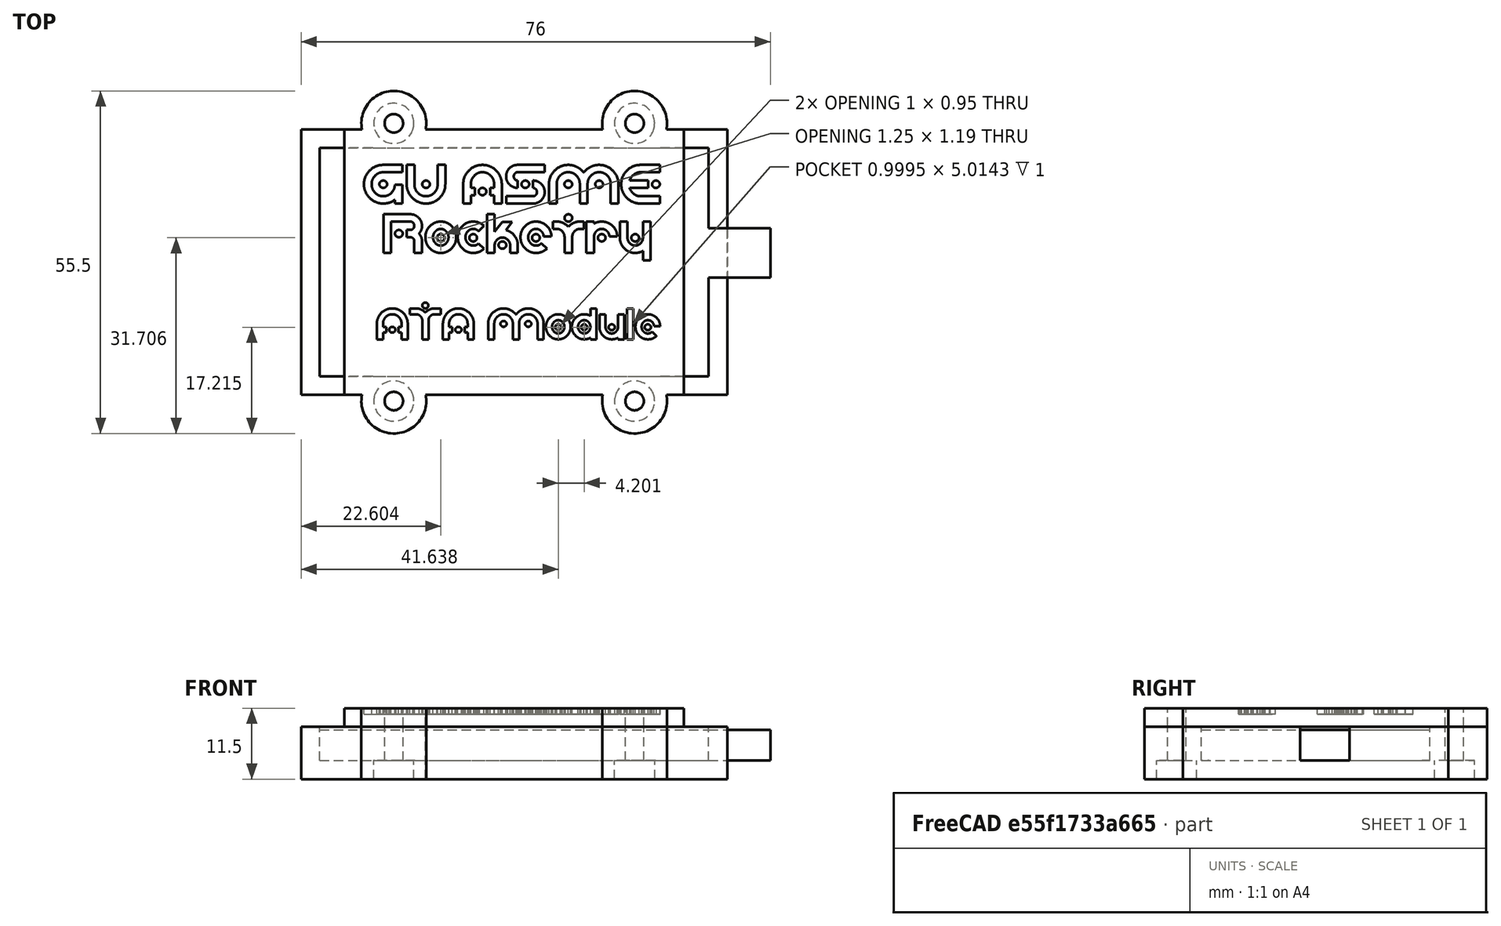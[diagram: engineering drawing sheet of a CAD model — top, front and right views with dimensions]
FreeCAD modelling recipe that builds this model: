
FCSTD DOCUMENT  (FreeCAD 0.19R)
Label: BatteryPlate
License: All rights reserved
LicenseURL: http://en.wikipedia.org/wiki/All_rights_reserved
objects: Part::Cylinder×32, Part::MultiFuse×18, Part::Cut×13, Part::Box×8, Part::Part2DObjectPython×3, Part::Extrusion×3
note: 77 computed .brp shape members not serialized (recipe doc carries the construction recipe); baked Part::Feature solids carry a one-line shape summary decoded from their .brp

FEATURE [Part::Box] Box  label="Cube"
  AttacherType = Attacher::AttachEngine3D
  Height = 6
  Length = 63
  Width = 37
FEATURE [Part::Box] Box001  label="Cube001"
  AttacherType = Attacher::AttachEngine3D
  Height = 6
  Length = 10
  Placement = pos=(63,16,0) rot=(0,0,1;0rad)
  Width = 8
FEATURE [Part::MultiFuse] Fusion  label="Battery Model"
  Placement = pos=(3,3,3) rot=(0,0,1;0rad)
  Shapes = -> [Box001,Box]
FEATURE [Part::Box] Box002  label="Cube002"
  AttacherType = Attacher::AttachEngine3D
  Height = 8.5
  Length = 69
  Width = 43
FEATURE [Part::Cut] Cut
  Base = -> Box002
  Tool = -> Fusion
FEATURE [Part::Box] Box003  label="Cube003"
  AttacherType = Attacher::AttachEngine3D
  Height = 5
  Length = 10
  Placement = pos=(63,16,0) rot=(0,0,1;0rad)
  Width = 8
FEATURE [Part::Box] Box004  label="Cube004"
  AttacherType = Attacher::AttachEngine3D
  Height = 5
  Length = 63
  Width = 37
FEATURE [Part::MultiFuse] Fusion001  label="Battery Model001"
  Placement = pos=(3,3,3) rot=(0,0,1;0rad)
  Shapes = -> [Box003,Box004]
FEATURE [Part::Cylinder] Cylinder008
  Angle = 360
  AttacherType = Attacher::AttachEngine3D
  Height = 8.5
  Placement = pos=(15,-1,0) rot=(0,0,1;0rad)
  Radius = 5.25
FEATURE [Part::Box] Box005  label="Lid Plate Base"
  AttacherType = Attacher::AttachEngine3D
  Height = 3
  Length = 55
  Placement = pos=(7,0,8.5) rot=(0,0,1;0rad)
  Width = 43
FEATURE [Part::Cylinder] Cylinder009  label="Screw Shaft"
  Angle = 360
  AttacherType = Attacher::AttachEngine3D
  Height = 8.5
  Placement = pos=(15,-1,0) rot=(0,0,1;0rad)
  Radius = 1.5
FEATURE [Part::Cylinder] Cylinder010  label="Nut Recess"
  Angle = 360
  AttacherType = Attacher::AttachEngine3D
  Height = 3
  Placement = pos=(15,-1,0) rot=(0,0,1;0rad)
  Radius = 3.25
FEATURE [Part::Cylinder] Cylinder012  label="Lid Flange Material"
  Angle = 360
  AttacherType = Attacher::AttachEngine3D
  Height = 3
  Placement = pos=(15,-1,8.5) rot=(0,0,1;0rad)
  Radius = 5.25
FEATURE [Part::MultiFuse] Fusion002  label="Base Bolt Assembly"
  Shapes = -> [Cylinder009,Cylinder010]
FEATURE [Part::Cut] Cut002  label="Base Bolt Flange - LL"
  Base = -> Cylinder008
  Tool = -> Fusion002
FEATURE [Part::Cylinder] Cylinder013  label="Screw Shaft001"
  Angle = 360
  AttacherType = Attacher::AttachEngine3D
  Height = 8.5
  Placement = pos=(15,-1,0) rot=(0,0,1;0rad)
  Radius = 1.5
FEATURE [Part::Cylinder] Cylinder014  label="Nut Recess001"
  Angle = 360
  AttacherType = Attacher::AttachEngine3D
  Height = 3
  Placement = pos=(15,-1,0) rot=(0,0,1;0rad)
  Radius = 3.25
FEATURE [Part::MultiFuse] Fusion003  label="Base Bolt Assembly001"
  Shapes = -> [Cylinder013,Cylinder014]
FEATURE [Part::Cylinder] Cylinder015
  Angle = 360
  AttacherType = Attacher::AttachEngine3D
  Height = 8.5
  Placement = pos=(15,-1,0) rot=(0,0,1;0rad)
  Radius = 5.25
FEATURE [Part::Cut] Cut004  label="Base Bolt Flange - LR"
  Base = -> Cylinder015
  Placement = pos=(39,0,0) rot=(0,0,1;0rad)
  Tool = -> Fusion003
FEATURE [Part::Cylinder] Cylinder016  label="Nut Recess002"
  Angle = 360
  AttacherType = Attacher::AttachEngine3D
  Height = 3
  Placement = pos=(15,-1,0) rot=(0,0,1;0rad)
  Radius = 3.25
FEATURE [Part::Cylinder] Cylinder017  label="Screw Shaft002"
  Angle = 360
  AttacherType = Attacher::AttachEngine3D
  Height = 8.5
  Placement = pos=(15,-1,0) rot=(0,0,1;0rad)
  Radius = 1.5
FEATURE [Part::Cylinder] Cylinder018
  Angle = 360
  AttacherType = Attacher::AttachEngine3D
  Height = 8.5
  Placement = pos=(15,-1,0) rot=(0,0,1;0rad)
  Radius = 5.25
FEATURE [Part::MultiFuse] Fusion004  label="Base Bolt Assembly002"
  Shapes = -> [Cylinder017,Cylinder016]
FEATURE [Part::Cut] Cut005  label="Base Bolt Flange - UR"
  Base = -> Cylinder018
  Placement = pos=(39,45,0) rot=(0,0,1;0rad)
  Tool = -> Fusion004
FEATURE [Part::Cylinder] Cylinder019
  Angle = 360
  AttacherType = Attacher::AttachEngine3D
  Height = 8.5
  Placement = pos=(15,-1,0) rot=(0,0,1;0rad)
  Radius = 5.25
FEATURE [Part::Cylinder] Cylinder020  label="Screw Shaft003"
  Angle = 360
  AttacherType = Attacher::AttachEngine3D
  Height = 8.5
  Placement = pos=(15,-1,0) rot=(0,0,1;0rad)
  Radius = 1.5
FEATURE [Part::Cylinder] Cylinder021  label="Nut Recess003"
  Angle = 360
  AttacherType = Attacher::AttachEngine3D
  Height = 3
  Placement = pos=(15,-1,0) rot=(0,0,1;0rad)
  Radius = 3.25
FEATURE [Part::MultiFuse] Fusion005  label="Base Bolt Assembly003"
  Shapes = -> [Cylinder020,Cylinder021]
FEATURE [Part::Cut] Cut006  label="Base Bolt Flange - UL"
  Base = -> Cylinder019
  Placement = pos=(0,45,0) rot=(0,0,1;0rad)
  Tool = -> Fusion005
FEATURE [Part::Cylinder] Cylinder022  label="Screw Shaft004"
  Angle = 360
  AttacherType = Attacher::AttachEngine3D
  Height = 8.5
  Placement = pos=(15,-1,0) rot=(0,0,1;0rad)
  Radius = 1.5
FEATURE [Part::Cylinder] Cylinder023  label="Nut Recess004"
  Angle = 360
  AttacherType = Attacher::AttachEngine3D
  Height = 3
  Placement = pos=(15,-1,0) rot=(0,0,1;0rad)
  Radius = 3.25
FEATURE [Part::MultiFuse] Fusion006  label="Base Bolt Assembly - LL"
  Shapes = -> [Cylinder022,Cylinder023]
FEATURE [Part::Cylinder] Cylinder024  label="Screw Shaft005"
  Angle = 360
  AttacherType = Attacher::AttachEngine3D
  Height = 8.5
  Placement = pos=(15,-1,0) rot=(0,0,1;0rad)
  Radius = 1.5
FEATURE [Part::Cylinder] Cylinder025  label="Nut Recess005"
  Angle = 360
  AttacherType = Attacher::AttachEngine3D
  Height = 3
  Placement = pos=(15,-1,0) rot=(0,0,1;0rad)
  Radius = 3.25
FEATURE [Part::MultiFuse] Fusion007  label="Base Bolt Assembly - LR"
  Placement = pos=(39,0,0) rot=(0,0,1;0rad)
  Shapes = -> [Cylinder024,Cylinder025]
FEATURE [Part::Cylinder] Cylinder026  label="Nut Recess006"
  Angle = 360
  AttacherType = Attacher::AttachEngine3D
  Height = 3
  Placement = pos=(15,-1,0) rot=(0,0,1;0rad)
  Radius = 3.25
FEATURE [Part::Cylinder] Cylinder027  label="Screw Shaft006"
  Angle = 360
  AttacherType = Attacher::AttachEngine3D
  Height = 8.5
  Placement = pos=(15,-1,0) rot=(0,0,1;0rad)
  Radius = 1.5
FEATURE [Part::MultiFuse] Fusion008  label="Base Bolt Assembly - UR"
  Placement = pos=(39,45,0) rot=(0,0,1;0rad)
  Shapes = -> [Cylinder027,Cylinder026]
FEATURE [Part::Cylinder] Cylinder028  label="Screw Shaft007"
  Angle = 360
  AttacherType = Attacher::AttachEngine3D
  Height = 8.5
  Placement = pos=(15,-1,0) rot=(0,0,1;0rad)
  Radius = 1.5
FEATURE [Part::Cylinder] Cylinder029  label="Nut Recess007"
  Angle = 360
  AttacherType = Attacher::AttachEngine3D
  Height = 3
  Placement = pos=(15,-1,0) rot=(0,0,1;0rad)
  Radius = 3.25
FEATURE [Part::MultiFuse] Fusion009  label="Base Bolt Assembly - UL"
  Placement = pos=(0,45,0) rot=(0,0,1;0rad)
  Shapes = -> [Cylinder028,Cylinder029]
FEATURE [Part::MultiFuse] Fusion010  label="Base Bolt Remove Assembly"
  Shapes = -> [Fusion009,Fusion006,Fusion007,Fusion008]
FEATURE [Part::Cut] Cut007
  Base = -> Cut
  Tool = -> Fusion010
FEATURE [Part::MultiFuse] Fusion011  label="Base Bolt Assemblies"
  Shapes = -> [Cut006,Cut005,Cut004,Cut002]
FEATURE [Part::Box] Box006  label="Cube005"
  AttacherType = Attacher::AttachEngine3D
  Height = 5.5
  Length = 10
  Placement = pos=(63,16,0) rot=(0,0,1;0rad)
  Width = 8
FEATURE [Part::Box] Box007  label="Cube006"
  AttacherType = Attacher::AttachEngine3D
  Height = 5.5
  Length = 63
  Width = 37
FEATURE [Part::MultiFuse] Fusion012  label="Battery Model002"
  Placement = pos=(3,3,3) rot=(0,0,1;0rad)
  Shapes = -> [Box006,Box007]
FEATURE [Part::Cut] Cut008  label="Base Bolt Assemblies - no Bat"
  Base = -> Fusion011
  Tool = -> Fusion012
FEATURE [Part::MultiFuse] Fusion013  label="Base Initial"
  Shapes = -> [Cut007,Cut008]
FEATURE [Part::Cylinder] Cylinder030  label="Lid Bolt Hole001"
  Angle = 360
  AttacherType = Attacher::AttachEngine3D
  Height = 3
  Placement = pos=(15,-1,8.5) rot=(0,0,1;0rad)
  Radius = 1.5
FEATURE [Part::Cylinder] Cylinder031  label="Lid Bolt Hole002"
  Angle = 360
  AttacherType = Attacher::AttachEngine3D
  Height = 3
  Placement = pos=(54,-1,8.5) rot=(0,0,1;0rad)
  Radius = 1.5
FEATURE [Part::Cylinder] Cylinder032  label="Lid Bolt Hole003"
  Angle = 360
  AttacherType = Attacher::AttachEngine3D
  Height = 3
  Placement = pos=(54,44,8.5) rot=(0,0,1;0rad)
  Radius = 1.5
FEATURE [Part::Cylinder] Cylinder033  label="Lid Bolt Hole004"
  Angle = 360
  AttacherType = Attacher::AttachEngine3D
  Height = 3
  Placement = pos=(15,44,8.5) rot=(0,0,1;0rad)
  Radius = 1.5
FEATURE [Part::MultiFuse] Fusion014  label="Lid Base Bolt Holes for Cut"
  Shapes = -> [Cylinder033,Cylinder030,Cylinder031,Cylinder032]
FEATURE [Part::Cylinder] Cylinder011  label="Lid Bolt Hole"
  Angle = 360
  AttacherType = Attacher::AttachEngine3D
  Height = 3
  Placement = pos=(15,-1,8.5) rot=(0,0,1;0rad)
  Radius = 1.5
FEATURE [Part::Cut] Cut001  label="Lid Bolt Flange - LL"
  Base = -> Cylinder012
  Tool = -> Cylinder011
FEATURE [Part::Cut] Cut009
  Base = -> Box005
  Tool = -> Fusion014
FEATURE [Part::Cylinder] Cylinder034  label="Lid Bolt Hole005"
  Angle = 360
  AttacherType = Attacher::AttachEngine3D
  Height = 3
  Placement = pos=(15,-1,8.5) rot=(0,0,1;0rad)
  Radius = 1.5
FEATURE [Part::Cylinder] Cylinder035  label="Lid Flange Material001"
  Angle = 360
  AttacherType = Attacher::AttachEngine3D
  Height = 3
  Placement = pos=(15,-1,8.5) rot=(0,0,1;0rad)
  Radius = 5.25
FEATURE [Part::Cut] Cut010  label="Lid Bolt Flange - LR"
  Base = -> Cylinder035
  Placement = pos=(39,0,0) rot=(0,0,1;0rad)
  Tool = -> Cylinder034
FEATURE [Part::Cylinder] Cylinder036  label="Lid Bolt Hole006"
  Angle = 360
  AttacherType = Attacher::AttachEngine3D
  Height = 3
  Placement = pos=(15,-1,8.5) rot=(0,0,1;0rad)
  Radius = 1.5
FEATURE [Part::Cylinder] Cylinder037  label="Lid Flange Material002"
  Angle = 360
  AttacherType = Attacher::AttachEngine3D
  Height = 3
  Placement = pos=(15,-1,8.5) rot=(0,0,1;0rad)
  Radius = 5.25
FEATURE [Part::Cut] Cut011  label="Lid Bolt Flange - UR"
  Base = -> Cylinder037
  Placement = pos=(39,45,0) rot=(0,0,1;0rad)
  Tool = -> Cylinder036
FEATURE [Part::Cylinder] Cylinder038  label="Lid Flange Material003"
  Angle = 360
  AttacherType = Attacher::AttachEngine3D
  Height = 3
  Placement = pos=(15,-1,8.5) rot=(0,0,1;0rad)
  Radius = 5.25
FEATURE [Part::Cylinder] Cylinder039  label="Lid Bolt Hole007"
  Angle = 360
  AttacherType = Attacher::AttachEngine3D
  Height = 3
  Placement = pos=(15,-1,8.5) rot=(0,0,1;0rad)
  Radius = 1.5
FEATURE [Part::Cut] Cut012  label="Lid Bolt Flange - UL"
  Base = -> Cylinder038
  Placement = pos=(0,45,0) rot=(0,0,1;0rad)
  Tool = -> Cylinder039
FEATURE [Part::MultiFuse] Fusion015  label="Lid Bolt Flanges"
  Shapes = -> [Cut001,Cut010,Cut011,Cut012]
FEATURE [Part::MultiFuse] Fusion016  label="Lid"
  Shapes = -> [Cut009,Fusion015]
FEATURE [Part::Part2DObjectPython] ShapeString  # Draft 2D object (typed FeaturePython)
  FontFile = <userpath>/fonts/SFPlanetaryOrbiter.ttf
  Placement = pos=(-50,20,0) rot=(0,0,1;0rad)
  Size = 5
  String = GU ASME
  Tracking = 0
FEATURE [Part::Part2DObjectPython] ShapeString001  # Draft 2D object (typed FeaturePython)
  FontFile = <userpath>/fonts/SFPlanetaryOrbiter.ttf
  Placement = pos=(-50,10,0) rot=(0,0,1;0rad)
  Size = 5
  String = Rocketry
  Tracking = 0
FEATURE [Part::Part2DObjectPython] ShapeString002  # Draft 2D object (typed FeaturePython)
  FontFile = <userpath>/fonts/SFPlanetaryOrbiter.ttf
  Placement = pos=(-50,0,0) rot=(0,0,1;0rad)
  Size = 4
  String = ATA Module
  Tracking = 0
FEATURE [Part::Extrusion] Extrude
  Base = -> ShapeString
  Dir = (0,0,1)
  DirMode = 2
  FaceMakerClass = Part::FaceMakerBullseye
  LengthFwd = 1
  LengthRev = 0
  Placement = pos=(60,11,10.5) rot=(0,0,1;0rad)
  Solid = false
  Symmetric = false
FEATURE [Part::Extrusion] Extrude001
  Base = -> ShapeString001
  Dir = (0,0,1)
  DirMode = 2
  FaceMakerClass = Part::FaceMakerBullseye
  LengthFwd = 1
  LengthRev = 0
  Placement = pos=(63,13,10.5) rot=(0,0,1;0rad)
  Solid = false
  Symmetric = false
FEATURE [Part::Extrusion] Extrude002
  Base = -> ShapeString002
  Dir = (0,0,1)
  DirMode = 2
  FaceMakerClass = Part::FaceMakerBullseye
  LengthFwd = 1
  LengthRev = 0
  Placement = pos=(62,9,10.5) rot=(0,0,1;0rad)
  Solid = false
  Symmetric = false
FEATURE [Part::MultiFuse] Fusion017  label="ATA Writing"
  Shapes = -> [Extrude,Extrude001,Extrude002]
FEATURE [Part::Cut] Cut013
  Base = -> Fusion016
  Tool = -> Fusion017
